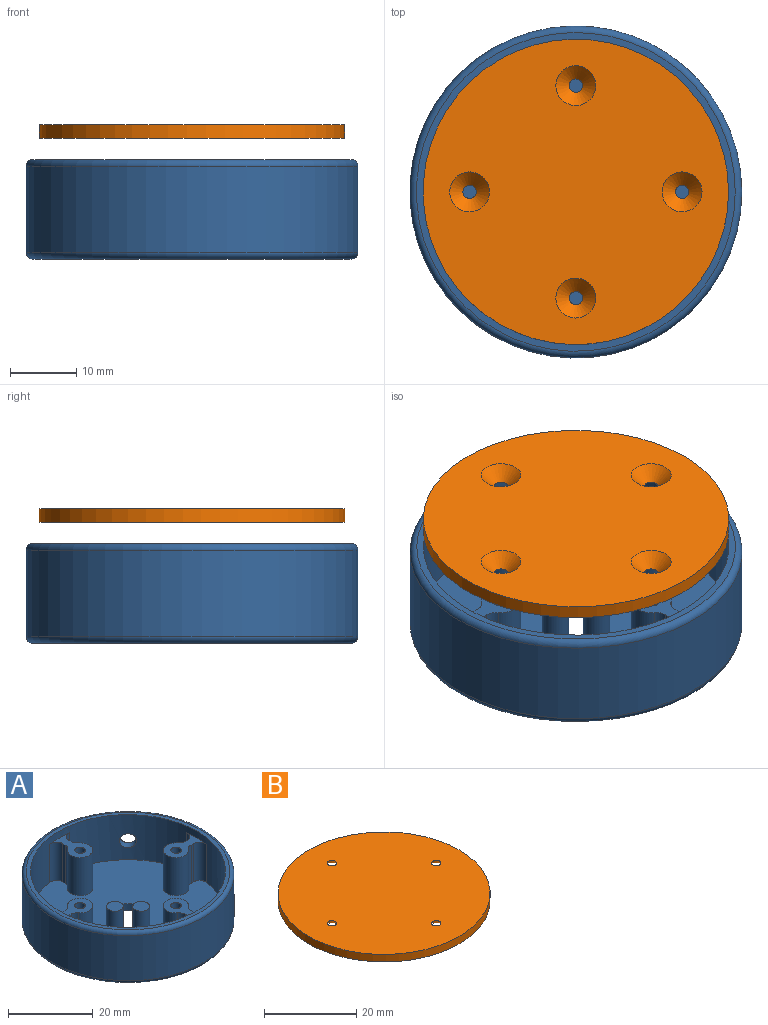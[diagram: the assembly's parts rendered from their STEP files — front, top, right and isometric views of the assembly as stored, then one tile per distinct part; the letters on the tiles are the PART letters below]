
ASSEMBLY  parts=2 mates=1
PART A: 53 faces, bbox 54.1x54.1x15 mm
  f0: cylinder r=25mm len=50mm, axis (0,0,-1), area 2029.4mm2, adj f46,f47,f52
  f1: cylinder r=23mm len=46mm, axis (0,0,1), area 1576mm2, adj f3,f7,f10,f11,f12,f13,f30,f33
  f2: cylinder r=3mm len=11mm, axis (0,0,-1), area 164.9mm2, adj f3,f13,f42,f43
  f3: plane 45.57x45.57mm, normal (0,0,1), area 1402.4mm2, adj f1,f2,f4,f5,f6,f9,f14,f15
  f4: cylinder r=3mm len=11mm, axis (0,0,-1), area 164.9mm2, adj f3,f11,f36,f37
  f5: cylinder r=3mm len=11mm, axis (0,0,-1), area 164.9mm2, adj f3,f12,f31,f32
  f6: cylinder r=3mm len=11mm, axis (0,0,-1), area 164.9mm2, adj f3,f10,f38,f41
  f7: plane 48x48mm, normal (0,0,1), area 147.7mm2, adj f1,f47
  f8: plane 48x48mm, normal (0,0,-1), area 1731mm2, adj f9,f46
  f9: cylinder r=5mm len=10mm, axis (0,0,-1), area 62.8mm2, adj f3,f8
  f10: plane 10x6.57mm, normal (0,0,1), area 34.1mm2, adj f1,f6,f14,f15,f28,f38,f39,f40
  f11: plane 10x6.57mm, normal (0,0,1), area 34.1mm2, adj f1,f4,f18,f19,f26,f34,f35,f36
  f12: plane 10x6.57mm, normal (0,0,1), area 34.1mm2, adj f1,f5,f16,f17,f24,f30,f31,f32
  f13: plane 10x6.57mm, normal (0,0,1), area 34.1mm2, adj f1,f2,f20,f21,f22,f42,f43,f44
  f14: plane 11x0.78mm, normal (1,0,0), area 8.6mm2, adj f3,f10,f38,f39
  f15: plane 11x0.78mm, normal (-1,0,0), area 8.6mm2, adj f3,f10,f40,f41
  f16: plane 11x0.78mm, normal (1,0,0), area 8.6mm2, adj f3,f12,f30,f31
  f17: plane 11x0.78mm, normal (-1,0,0), area 8.6mm2, adj f3,f12,f32,f33
  f18: plane 11x0.78mm, normal (0,1,0), area 8.6mm2, adj f3,f11,f35,f36
  f19: plane 11x0.78mm, normal (0,-1,0), area 8.6mm2, adj f3,f11,f34,f37
  f20: plane 11x0.78mm, normal (0,-1,0), area 8.6mm2, adj f3,f13,f42,f45
  f21: plane 11x0.78mm, normal (0,1,0), area 8.6mm2, adj f3,f13,f43,f44
  f22: cylinder r=1.25mm len=10mm, axis (0,0,1), area 78.5mm2, adj f13,f23
  f23: plane 2.5x2.5mm, normal (0,0,1), area 4.9mm2, adj f22
  f24: cylinder r=1.25mm len=10mm, axis (0,0,1), area 78.5mm2, adj f12,f25
  f25: plane 2.5x2.5mm, normal (0,0,1), area 4.9mm2, adj f24
  f26: cylinder r=1.25mm len=10mm, axis (0,0,1), area 78.5mm2, adj f11,f27
  f27: plane 2.5x2.5mm, normal (0,0,1), area 4.9mm2, adj f26
  f28: cylinder r=1.25mm len=10mm, axis (0,0,1), area 78.5mm2, adj f10,f29
  f29: plane 2.5x2.5mm, normal (0,0,1), area 4.9mm2, adj f28
  f30: cylinder r=2mm len=11mm, axis (0,0,1), area 37.7mm2, adj f1,f3,f12,f16
  f31: cylinder r=2mm len=11mm, axis (0,0,-1), area 20.4mm2, adj f3,f5,f12,f16
  f32: cylinder r=2mm len=11mm, axis (0,0,-1), area 20.4mm2, adj f3,f5,f12,f17
  f33: cylinder r=2mm len=11mm, axis (0,0,1), area 37.7mm2, adj f1,f3,f12,f17
  f34: cylinder r=2mm len=11mm, axis (0,0,1), area 37.7mm2, adj f1,f3,f11,f19
  f35: cylinder r=2mm len=11mm, axis (0,0,1), area 37.7mm2, adj f1,f3,f11,f18
  f36: cylinder r=2mm len=11mm, axis (0,0,-1), area 20.4mm2, adj f3,f4,f11,f18
  f37: cylinder r=2mm len=11mm, axis (0,0,-1), area 20.4mm2, adj f3,f4,f11,f19
  f38: cylinder r=2mm len=11mm, axis (0,0,-1), area 20.4mm2, adj f3,f6,f10,f14
  f39: cylinder r=2mm len=11mm, axis (0,0,1), area 37.7mm2, adj f1,f3,f10,f14
  f40: cylinder r=2mm len=11mm, axis (0,0,1), area 37.7mm2, adj f1,f3,f10,f15
  f41: cylinder r=2mm len=11mm, axis (0,0,-1), area 20.4mm2, adj f3,f6,f10,f15
  f42: cylinder r=2mm len=11mm, axis (0,0,-1), area 20.4mm2, adj f2,f3,f13,f20
  f43: cylinder r=2mm len=11mm, axis (0,0,-1), area 20.4mm2, adj f2,f3,f13,f21
  f44: cylinder r=2mm len=11mm, axis (0,0,1), area 37.7mm2, adj f1,f3,f13,f21
  f45: cylinder r=2mm len=11mm, axis (0,0,1), area 37.7mm2, adj f1,f3,f13,f20
  f46: torus R=24mm, axis (0,0,1), area 243.2mm2, adj f0,f8
  f47: torus R=24mm, axis (0,0,1), area 243.2mm2, adj f0,f7
  f48: plane 4x4mm, normal (0,0,1), area 12.6mm2, adj f49
  f49: cylinder r=2mm len=11mm, axis (0,0,-1), area 138.2mm2, adj f3,f48
  f50: plane 4x4mm, normal (0,0,1), area 12.6mm2, adj f51
  f51: cylinder r=2mm len=11mm, axis (0,0,-1), area 138.2mm2, adj f3,f50
  f52: cylinder r=2mm len=4.3mm, axis (-0.71,-0.71,0), area 25.2mm2, adj f0,f1
PART B: 7 faces, bbox 46x46x2 mm
  f0: cylinder r=23mm len=46mm, axis (0,0,-1), area 289mm2, adj f1,f2
  f1: plane 46x46mm, normal (0,0,1), area 1649.3mm2, adj f0,f3,f4,f5,f6
  f2: plane 46x46mm, normal (0,0,-1), area 1548.8mm2, adj f0,f3,f4,f5,f6
  f3: cone r=1mm half-angle=45deg, axis (0,0,-1), area 35.5mm2, adj f1,f2
  f4: cone r=1mm half-angle=45deg, axis (0,0,-1), area 35.5mm2, adj f1,f2
  f5: cone r=1mm half-angle=45deg, axis (0,0,-1), area 35.5mm2, adj f1,f2
  f6: cone r=1mm half-angle=45deg, axis (0,0,-1), area 35.5mm2, adj f1,f2
PLACE A t=(-24.95,-1.35,-5.82)mm fixed
PLACE B rot(axis=(1,0,0),180deg) t=(-24.95,-1.35,14.41)mm
MATE slider B.f5 <-> A.f6  axis (0,0,1) through (-24.95,14.65,14.41)mm
